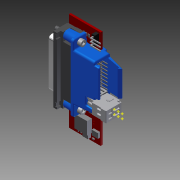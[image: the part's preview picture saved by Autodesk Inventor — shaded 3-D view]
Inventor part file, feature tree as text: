
AUTODESK INVENTOR PART (.ipt)
format: ipt  version: 2011 (Build 150239000, 239)  size: 3,314,176 bytes
history: native  units: in
note: dims shown in document units (in); Inventor stores cm internally (conversion verified against a paired STEP export)
features: other x30, plane x4, sketch x2
ambient origin geometry x8: Origin, YZ Plane, XZ Plane, XY Plane, X Axis, Y Axis, Z Axis, Center Point
bodies: Solid1 (feature_tree)
feature tree (36):
  other  "Analog Breakout Assembly.iam"
  other  "Analog Breakout Board Assembly.iam:1::Analog Board Rev2.ipt:1"
  other  "Analog Breakout Board Assembly.iam:1::SOD-123_0_0531_D.ipt:1"
  other  "Analog Breakout Board Assembly.iam:1::R0805_M_0_0236_R.ipt:1"
  other  "Analog Breakout Board Assembly.iam:1::LED1208RA_LiteOn_0_0394_D.ipt:1"
  other  "Analog Breakout Board Assembly.iam:1::R0805_M_0_0236_R.ipt:2"
  other  "Analog Breakout Board Assembly.iam:1::R0805_M_0_0236_R.ipt:3"
  other  "Analog Breakout Board Assembly.iam:1::TPS543X_0_0661_U.ipt:1"
  other  "Analog Breakout Board Assembly.iam:1::R0603_C_0_0236_R.ipt:1"
  other  "Analog Breakout Board Assembly.iam:1::R0603_C_0_0236_R.ipt:2"
  other  "Analog Breakout Board Assembly.iam:1::CoilCraft_MSS1038_0_1496_L.ipt:1"
  other  "Analog Breakout Board Assembly.iam:1::SMA_0_0949_D.ipt:1"
  other  "Analog Breakout Board Assembly.iam:1::SMT-CAN_Nippon_F80_0_3031_C.ipt:1"
  other  "Analog Breakout Board Assembly.iam:1::C0603_C_0_0354_C.ipt:1"
  other  "Analog Breakout Board Assembly.iam:1::734-162:1"
  other  "Analog Breakout Board Assembly.iam:1::C-5747846-02-3.ipt:1"
  other  "Analog Breakout Board Assembly.iam:1::Samtec 8x3 RA Connector.ipt:1"
  other  "Analog Muzzle Rev2.ipt:1"
  other  "4-40 SHCS.ipt:1"
  other  "4-40 SHCS.ipt:2"
  other  "Jumper 3 Pin RA.ipt:1"
  other  "Analog Breakout Assembly.iam_Bodies"
  sketch  "Sketch2"  dims[d0=0.3937in]
  sketch  "Sketch3"  dims[d1=0.125in d2=0.25in d3=0.125in d4=0.25in]
  other  "Work Point3"
  other  "Work Point4"
  other  "Work Point5"
  other  "Work Point6"
  plane  "Work Plane1"
  other  "Work Axis1"
  plane  "Work Plane2"
  other  "Work Axis2"
  plane  "Work Plane3"
  other  "Work Axis3"
  plane  "Work Plane4"
  other  "Work Axis4"
